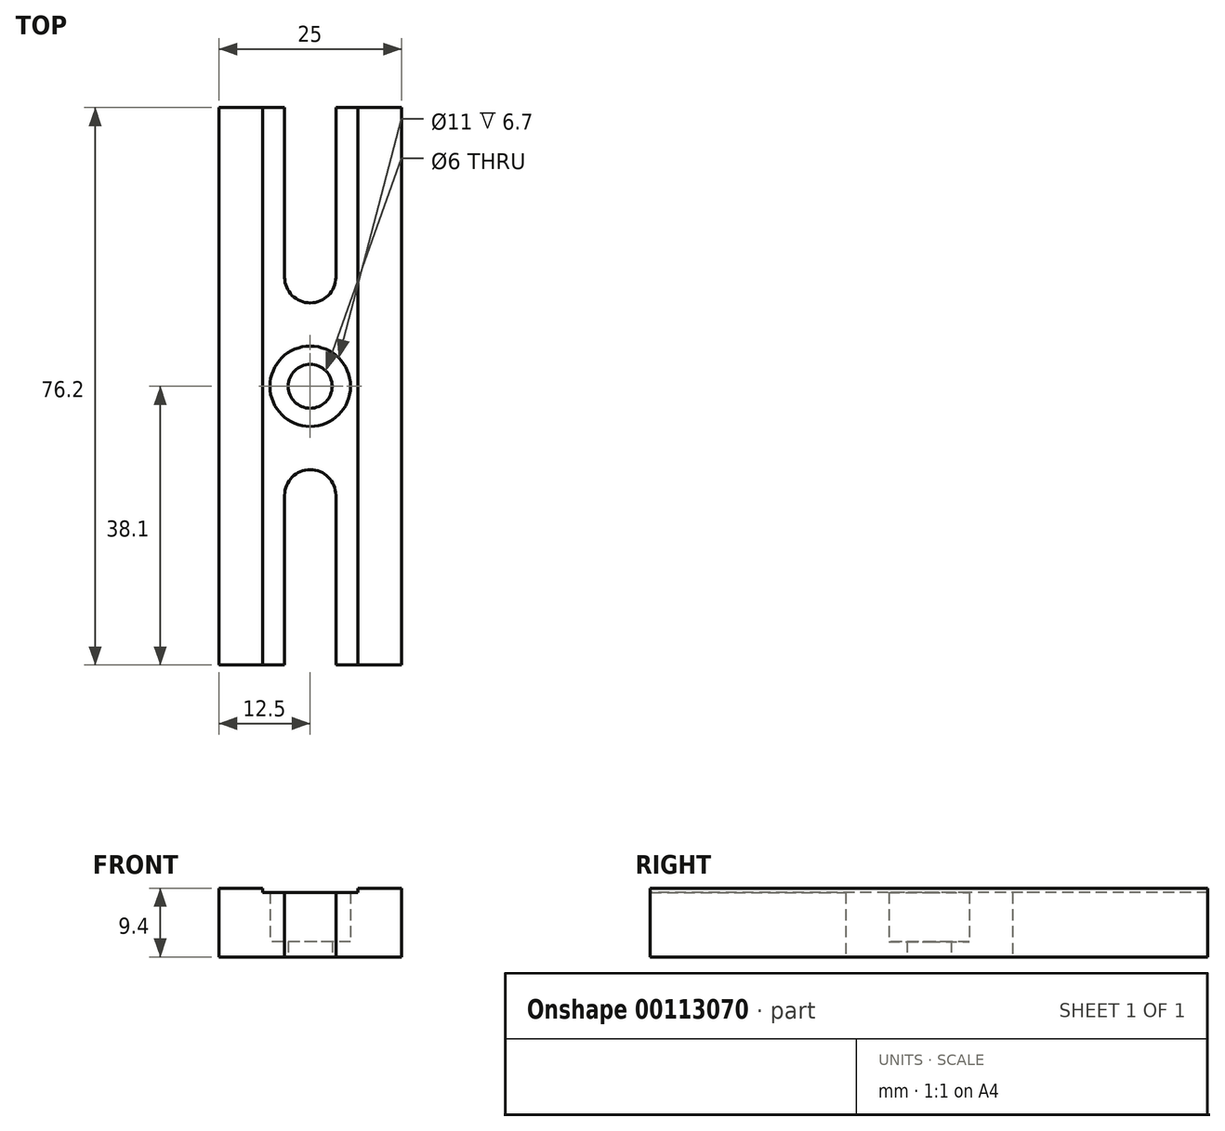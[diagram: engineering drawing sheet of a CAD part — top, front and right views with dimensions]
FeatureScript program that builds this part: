
annotation { "Feature Type Name" : "Feature", "Feature Type Description" : "" }
export const myFeature = defineFeature(function(context is Context, id is Id, definition is map)
    precondition{}
    {
        {
            var Q0;
            Q0=qCreatedBy(makeId("Top.planeOp"),FACE);
            var sketch = newSketch(context, id + "F0", { "sketchPlane" : qUnion([Q0])});
            skLineSegment(sketch, "E0.bottom", {"start": v(12.5, -38.1) * mm, "end": v(-12.5, -38.1) * mm});
            skLineSegment(sketch, "E0.top", {"start": v(12.5, 38.1) * mm, "end": v(-12.5, 38.1) * mm});
            skLineSegment(sketch, "E0.left", {"start": v(12.5, -38.1) * mm, "end": v(12.5, 38.1) * mm});
            skLineSegment(sketch, "E0.right", {"start": v(-12.5, -38.1) * mm, "end": v(-12.5, 38.1) * mm});
            skPoint(sketch, "E0.middle", {"position": v(0, 0) * mm});
            skLineSegment(sketch, "E1", {"start": v(-12.5, 0) * mm, "end": v(12.5, 0) * mm, "construction": true});
            skLineSegment(sketch, "E2", {"start": v(-3.5, 38.1) * mm, "end": v(-3.5, 14.9) * mm});
            skLineSegment(sketch, "E3", {"start": v(3.5, 38.1) * mm, "end": v(3.5, 14.9) * mm});
            skArc(sketch, "E4", {"start": v(-3.5, 14.9) * mm, "mid": v(0, 11.4) * mm, "end": v(3.5, 14.9) * mm});
            skCircle(sketch, "E5", {"center": v(0, 0) * mm, "radius": 5.5 * mm});
            skCircle(sketch, "E6", {"center": v(0, 0) * mm, "radius": 3 * mm});
            skLineSegment(sketch, "E7.MirrorCS", {"start": v(-3.5, -38.1) * mm, "end": v(-3.5, -14.9) * mm});
            skArc(sketch, "E8.MirrorCS", {"start": v(-3.5, -14.9) * mm, "mid": v(0, -11.4) * mm, "end": v(3.5, -14.9) * mm});
            skLineSegment(sketch, "E9.MirrorCS", {"start": v(3.5, -38.1) * mm, "end": v(3.5, -14.9) * mm});
            skSolve(sketch);
        }
        {
            var Q0;
            {var subQ3=sQuery(id+"F0.wireOp",EDGE,"E0.left");Q0=makeQuery(id+"F0.imprint","IMPRINT",FACE,{"disambiguationData":[TD([[makeQuery(id+"F0.imprint","IMPRINT",EDGE,{"derivedFrom":subQ3}),1.0]])]});}
            extrude(context, id + "F1", {"entities" : qUnion([Q0]), "depth" : 9.4 * mm});
        }
        {
            var Q0;
            Q0=makeQuery(id+"F0.imprint","IMPRINT",FACE,{"disambiguationData":[TD([[makeQuery(id+"F0.imprint","IMPRINT",EDGE,{"derivedFrom":sQuery(id+"F0.wireOp",EDGE,"E5")}),1.0]])]});
            extrude(context, id + "F2", {"entities" : qUnion([Q0]), "operationType" : NewBodyOperationType.ADD, "depth" : 2.1 * mm});
        }
        {
            var Q0;
            Q0=makeQuery(id+"F1.opExtrude","CAP_FACE",FACE,{"disambiguationData":[OSD([sQuery(id+"F0.wireOp",EDGE,"E0.bottom"),sQuery(id+"F0.wireOp",EDGE,"E0.top"),sQuery(id+"F0.wireOp",EDGE,"E0.left"),sQuery(id+"F0.wireOp",EDGE,"E0.right"),sQuery(id+"F0.wireOp",EDGE,"E2"),sQuery(id+"F0.wireOp",EDGE,"E3"),sQuery(id+"F0.wireOp",EDGE,"E4"),sQuery(id+"F0.wireOp",EDGE,"E5"),sQuery(id+"F0.wireOp",EDGE,"E7.MirrorCS"),sQuery(id+"F0.wireOp",EDGE,"E8.MirrorCS"),sQuery(id+"F0.wireOp",EDGE,"E9.MirrorCS")])],"isStart":false});
            var sketch = newSketch(context, id + "F3", { "sketchPlane" : qUnion([Q0])});
            skLineSegment(sketch, "E10.bottom", {"start": v(6.5, 38.1) * mm, "end": v(-6.5, 38.1) * mm});
            skLineSegment(sketch, "E10.top", {"start": v(6.5, -38.1) * mm, "end": v(-6.5, -38.1) * mm});
            skLineSegment(sketch, "E10.left", {"start": v(6.5, 38.1) * mm, "end": v(6.5, -38.1) * mm});
            skLineSegment(sketch, "E10.right", {"start": v(-6.5, 38.1) * mm, "end": v(-6.5, -38.1) * mm});
            skPoint(sketch, "E10.middle", {"position": v(0, 0) * mm});
            skSolve(sketch);
        }
        {
            var Q0;
            {var subQ5=sQuery(id+"F3.wireOp",EDGE,"E10.left");Q0=makeQuery(id+"F3.imprint","IMPRINT",FACE,{"disambiguationData":[TD([[makeQuery(id+"F3.imprint","IMPRINT",EDGE,{"derivedFrom":subQ5}),-1.0]])]});}
            extrude(context, id + "F4", {"entities" : qUnion([Q0]), "operationType" : NewBodyOperationType.REMOVE, "oppositeDirection" : true, "depth" : 0.6 * mm});
        }
    });
